# Revit family: EDE-SNT-ITP-SANITARIO TWO PIECES_ EVOLUTION R CON ASTO BLANCO
name_source: partatom
category: Aparatos sanitarios
units: mm (PartAtom-declared; Revit-internal decimal feet)

## family parameters
Compartido = Sí
Corte con vacíos al cargar = No
Cota de conector redondo = Diámetro de uso
Número OmniClass = 23.45.00.00
Punto de cálculo de habitación = Sí
Se basa en plano de trabajo = No
Siempre vertical = Sí
Tipo de pieza = Normal
Título OmniClass = Sanitary, Laundry, and Cleaning Equipment

## types (1)
- INODORO EVOLUTION REDONDO
    Conexión AC = Sí
    Conexión AF = Sí
    Conexión de residuos = Sí
    Conexión de ventilación = Sí
    Fabricante = EDESA Ecuador
    Imagen de tipo = <Ninguno>
    Modelo = INODORO EVOLUTION REDONDO CON ASIENTO BLANCO
    URL = https://www.edesa.com.ec
    _ALT_Basamento = 0.4 m
    _ALT_Eje instalación = 0.6 m
    _EDESA_ Alto en cm = 74.4
    _EDESA_ Ancho en cm = 42.4
    _EDESA_ Categoría = Productos > Sanitarios > Inodoros > Two Pieces
    _EDESA_ Certificación = Cumple con norma NTE INEN 3082
    _EDESA_ Color = blanco, bone, vison, azul galaxie, pink, navy blue, verde teal, cherry, negro, verde pistacho, orange, rojo
    _EDESA_ Conexión hidráulica = Entrada de agua: tubería ø 1/2" Salida de agua: tubería ø 4"
    _EDESA_ Consumo/capacidad de agua en L = 6.0 litros
    _EDESA_ Descripción = Inodoro de dos piezas redondo con tanque alto, sistema de una descarga superior y asiento de caída libre.
    _EDESA_ Distancia de instalación en cm (muro terminado) = 30.5 cm
    _EDESA_ Garantía = De por vida en funcionamiento y acabado de la cerámica sanitaria
    _EDESA_ Manual de instalación = https://www.edesa.com.ec
    _EDESA_ Marca = EDESA
    _EDESA_ Materiales = Cerámica Sanitaria
    _EDESA_ Nombre = INODORO EVOLUTION REDONDO CON ASIENTO BLANCO
    _EDESA_ Peso en kg = 30.2 kg
    _EDESA_ Productos incluídos = Herraje Universal, Asiento redondo, Push Button superior
    _EDESA_ Productos necesarios para instalación = Llave angular y manguera flexible, sello de cera, Set de anclaje taza piso, Tapas de Anclaje
    _EDESA_ Profundidad en cm = 68
    _EDESA_ Sku/código = JS002291___1CE
    _EDESA_ Tipo de instalación = Al piso
